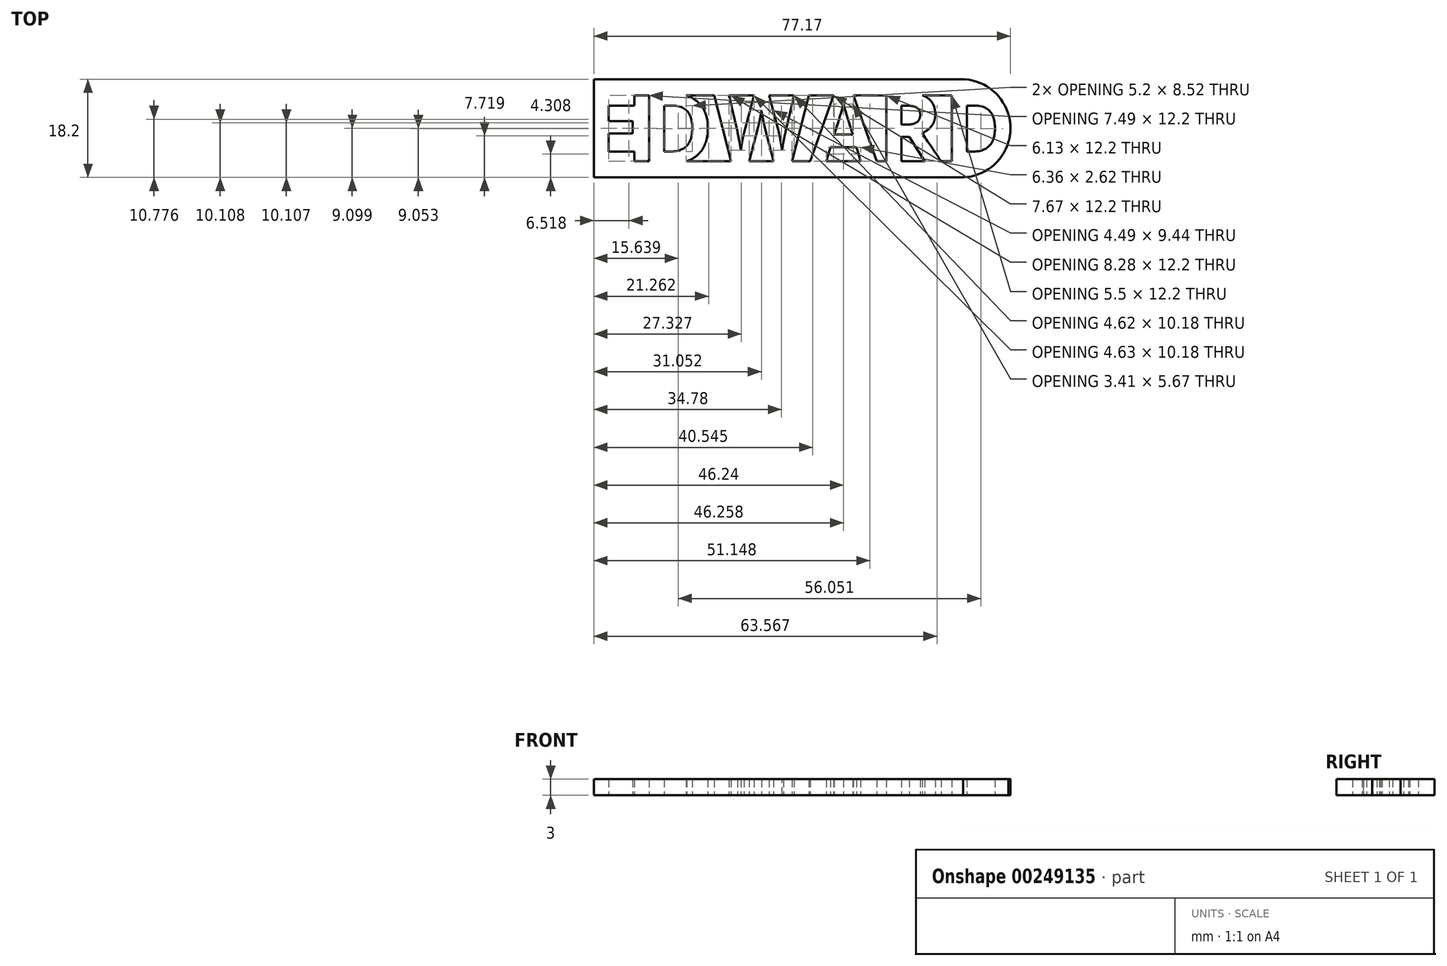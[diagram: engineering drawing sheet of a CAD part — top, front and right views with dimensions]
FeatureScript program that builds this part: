
annotation { "Feature Type Name" : "Feature", "Feature Type Description" : "" }
export const myFeature = defineFeature(function(context is Context, id is Id, definition is map)
    precondition{}
    {
        {
            var Q0;
            Q0=qCreatedBy(makeId("Top.planeOp"),FACE);
            var sketch = newSketch(context, id + "F0", { "sketchPlane" : qUnion([Q0])});
            skText(sketch, "E0", { "text": "EDWARD", "fontName": "OpenSans-Bold.ttf"});
            skLineSegment(sketch, "E1.bottom", {"start": v(-40, 0.5) * mm, "end": v(40, 0.5) * mm});
            skLineSegment(sketch, "E1.top", {"start": v(-40, -2.5) * mm, "end": v(40, -2.5) * mm});
            skLineSegment(sketch, "E1.left", {"start": v(-40, -2.5) * mm, "end": v(-40, 0.5) * mm});
            skLineSegment(sketch, "E1.right", {"start": v(40, -2.5) * mm, "end": v(40, 0.5) * mm});
            skLineSegment(sketch, "E2.bottom", {"start": v(-40, 12.7) * mm, "end": v(40, 12.7) * mm});
            skLineSegment(sketch, "E2.top", {"start": v(-40, 15.7) * mm, "end": v(40, 15.7) * mm});
            skLineSegment(sketch, "E2.left", {"start": v(-40, 12.7) * mm, "end": v(-40, 15.7) * mm});
            skLineSegment(sketch, "E2.right", {"start": v(40, 12.7) * mm, "end": v(40, 15.7) * mm});
            const initialGuessF0  = {"E0": [-0.04, 0, 1, 0, 0.0132]};
            skSetInitialGuess(sketch, initialGuessF0);
            skSolve(sketch);
        }
        {
            var Q0;
            {var subQ0=sQuery(id+"F0.wireOp",EDGE,"E0.sketch_text.stroke-0");Q0=makeQuery(id+"F0.imprint","IMPRINT",FACE,{"disambiguationData":[TD([[makeQuery(id+"F0.imprint","IMPRINT",EDGE,{"derivedFrom":subQ0}),-1.0]])]});}
            var Q1;
            {var subQ8=sQuery(id+"F0.wireOp",EDGE,"E0.sketch_text.stroke-4");Q1=makeQuery(id+"F0.imprint","IMPRINT",FACE,{"disambiguationData":[TD([[makeQuery(id+"F0.imprint","IMPRINT",EDGE,{"derivedFrom":subQ8}),-1.0]])]});}
            var Q2;
            {var subQ27=sQuery(id+"F0.wireOp",EDGE,"E0.sketch_text.stroke-0");Q2=makeQuery(id+"F0.imprint","IMPRINT",FACE,{"disambiguationData":[TD([[makeQuery(id+"F0.imprint","IMPRINT",EDGE,{"derivedFrom":subQ27}),1.0]])]});}
            var Q3;
            {var subQ1=sQuery(id+"F0.wireOp",EDGE,"E0.sketch_text.stroke-12");Q3=makeQuery(id+"F0.imprint","IMPRINT",FACE,{"disambiguationData":[TD([[makeQuery(id+"F0.imprint","IMPRINT",EDGE,{"derivedFrom":subQ1}),-1.0]])]});}
            var Q4;
            {var subQ0=sQuery(id+"F0.wireOp",EDGE,"E0.sketch_text.stroke-14");Q4=makeQuery(id+"F0.imprint","IMPRINT",FACE,{"disambiguationData":[TD([[makeQuery(id+"F0.imprint","IMPRINT",EDGE,{"derivedFrom":subQ0}),-1.0]])]});}
            var Q5;
            {var subQ11=sQuery(id+"F0.wireOp",EDGE,"E0.sketch_text.stroke-26");Q5=makeQuery(id+"F0.imprint","IMPRINT",FACE,{"disambiguationData":[TD([[makeQuery(id+"F0.imprint","IMPRINT",EDGE,{"derivedFrom":subQ11}),-1.0]])]});}
            var Q6;
            {var subQ0=sQuery(id+"F0.wireOp",EDGE,"E0.sketch_text.stroke-31");Q6=makeQuery(id+"F0.imprint","IMPRINT",FACE,{"disambiguationData":[TD([[makeQuery(id+"F0.imprint","IMPRINT",EDGE,{"derivedFrom":subQ0}),-1.0]])]});}
            var Q7;
            {var subQ0=sQuery(id+"F0.wireOp",EDGE,"E0.sketch_text.stroke-24");Q7=makeQuery(id+"F0.imprint","IMPRINT",FACE,{"disambiguationData":[TD([[makeQuery(id+"F0.imprint","IMPRINT",EDGE,{"derivedFrom":subQ0}),-1.0]])]});}
            var Q8;
            {var subQ5=sQuery(id+"F0.wireOp",EDGE,"E0.sketch_text.stroke-49");Q8=makeQuery(id+"F0.imprint","IMPRINT",FACE,{"disambiguationData":[TD([[makeQuery(id+"F0.imprint","IMPRINT",EDGE,{"derivedFrom":subQ5}),-1.0]])]});}
            var Q9;
            {var subQ0=sQuery(id+"F0.wireOp",EDGE,"E0.sketch_text.stroke-51");Q9=makeQuery(id+"F0.imprint","IMPRINT",FACE,{"disambiguationData":[TD([[makeQuery(id+"F0.imprint","IMPRINT",EDGE,{"derivedFrom":subQ0}),-1.0]])]});}
            var Q10;
            {var subQ0=sQuery(id+"F0.wireOp",EDGE,"E0.sketch_text.stroke-55");Q10=makeQuery(id+"F0.imprint","IMPRINT",FACE,{"disambiguationData":[TD([[makeQuery(id+"F0.imprint","IMPRINT",EDGE,{"derivedFrom":subQ0}),-1.0]])]});}
            var Q11;
            Q11=makeQuery(id+"F0.imprint","IMPRINT",FACE,{"disambiguationData":[TD([[makeQuery(id+"F0.imprint","IMPRINT",EDGE,{"derivedFrom":sQuery(id+"F0.wireOp",EDGE,"E0.sketch_text.stroke-60")}),-1.0]])]});
            var Q12;
            {var subQ0=sQuery(id+"F0.wireOp",EDGE,"E0.sketch_text.stroke-68");Q12=makeQuery(id+"F0.imprint","IMPRINT",FACE,{"disambiguationData":[TD([[makeQuery(id+"F0.imprint","IMPRINT",EDGE,{"derivedFrom":subQ0}),-1.0]])]});}
            var Q13;
            {var subQ0=sQuery(id+"F0.wireOp",EDGE,"E0.sketch_text.stroke-76");Q13=makeQuery(id+"F0.imprint","IMPRINT",FACE,{"disambiguationData":[TD([[makeQuery(id+"F0.imprint","IMPRINT",EDGE,{"derivedFrom":subQ0}),-1.0]])]});}
            var Q14;
            {var subQ0=sQuery(id+"F0.wireOp",EDGE,"E0.sketch_text.stroke-81");Q14=makeQuery(id+"F0.imprint","IMPRINT",FACE,{"disambiguationData":[TD([[makeQuery(id+"F0.imprint","IMPRINT",EDGE,{"derivedFrom":subQ0}),-1.0]])]});}
            var Q15;
            {var subQ1=sQuery(id+"F0.wireOp",EDGE,"E0.sketch_text.stroke-79");Q15=makeQuery(id+"F0.imprint","IMPRINT",FACE,{"disambiguationData":[TD([[makeQuery(id+"F0.imprint","IMPRINT",EDGE,{"derivedFrom":subQ1}),-1.0]])]});}
            var Q16;
            {var subQ37=sQuery(id+"F0.wireOp",EDGE,"E0.sketch_text.stroke-2");Q16=makeQuery(id+"F0.imprint","IMPRINT",FACE,{"disambiguationData":[TD([[makeQuery(id+"F0.imprint","IMPRINT",EDGE,{"derivedFrom":subQ37}),1.0]])]});}
            var Q17;
            {var subQ0=sQuery(id+"F0.wireOp",EDGE,"E0.sketch_text.stroke-83");Q17=makeQuery(id+"F0.imprint","IMPRINT",FACE,{"disambiguationData":[TD([[makeQuery(id+"F0.imprint","IMPRINT",EDGE,{"derivedFrom":subQ0}),-1.0]])]});}
            var Q18;
            {var subQ0=sQuery(id+"F0.wireOp",EDGE,"E0.sketch_text.stroke-70");Q18=makeQuery(id+"F0.imprint","IMPRINT",FACE,{"disambiguationData":[TD([[makeQuery(id+"F0.imprint","IMPRINT",EDGE,{"derivedFrom":subQ0}),-1.0]])]});}
            var Q19;
            {var subQ0=sQuery(id+"F0.wireOp",EDGE,"E0.sketch_text.stroke-53");Q19=makeQuery(id+"F0.imprint","IMPRINT",FACE,{"disambiguationData":[TD([[makeQuery(id+"F0.imprint","IMPRINT",EDGE,{"derivedFrom":subQ0}),-1.0]])]});}
            var Q20;
            {var subQ0=sQuery(id+"F0.wireOp",EDGE,"E0.sketch_text.stroke-46");Q20=makeQuery(id+"F0.imprint","IMPRINT",FACE,{"disambiguationData":[TD([[makeQuery(id+"F0.imprint","IMPRINT",EDGE,{"derivedFrom":subQ0}),-1.0]])]});}
            var Q21;
            {var subQ0=sQuery(id+"F0.wireOp",EDGE,"E0.sketch_text.stroke-39");Q21=makeQuery(id+"F0.imprint","IMPRINT",FACE,{"disambiguationData":[TD([[makeQuery(id+"F0.imprint","IMPRINT",EDGE,{"derivedFrom":subQ0}),-1.0]])]});}
            var Q22;
            {var subQ0=sQuery(id+"F0.wireOp",EDGE,"E0.sketch_text.stroke-33");Q22=makeQuery(id+"F0.imprint","IMPRINT",FACE,{"disambiguationData":[TD([[makeQuery(id+"F0.imprint","IMPRINT",EDGE,{"derivedFrom":subQ0}),-1.0]])]});}
            var Q23;
            {var subQ0=sQuery(id+"F0.wireOp",EDGE,"E0.sketch_text.stroke-16");Q23=makeQuery(id+"F0.imprint","IMPRINT",FACE,{"disambiguationData":[TD([[makeQuery(id+"F0.imprint","IMPRINT",EDGE,{"derivedFrom":subQ0}),-1.0]])]});}
            var Q24;
            {var subQ0=sQuery(id+"F0.wireOp",EDGE,"E0.sketch_text.stroke-2");Q24=makeQuery(id+"F0.imprint","IMPRINT",FACE,{"disambiguationData":[TD([[makeQuery(id+"F0.imprint","IMPRINT",EDGE,{"derivedFrom":subQ0}),-1.0]])]});}
            extrude(context, id + "F1", {"entities" : qUnion([Q0, Q1, Q2, Q3, Q4, Q5, Q6, Q7, Q8, Q9, Q10, Q11, Q12, Q13, Q14, Q15, Q16, Q17, Q18, Q19, Q20, Q21, Q22, Q23, Q24]), "depth" : 2 * mm});
        }
        {
            var Q0;
            Q0=makeQuery(id+"F1.opExtrude","SWEPT_FACE",FACE,{"disambiguationData":[OSD([sQuery(id+"F0.wireOp",EDGE,"E2.left")])]});
            var Q1;
            Q1=makeQuery(id+"F1.opExtrude","SWEPT_FACE",FACE,{"disambiguationData":[OSD([sQuery(id+"F0.wireOp",EDGE,"E0.sketch_text.stroke-1")])]});
            extrude(context, id + "F2", {"entities" : qUnion([Q0]), "operationType" : NewBodyOperationType.REMOVE, "endBound" : BoundingType.UP_TO_SURFACE, "oppositeDirection" : true, "endBoundEntityFace" : qUnion([Q1]), "depth" : 25 * mm});
        }
        {
            var Q0;
            Q0=makeQuery(id+"F1.opExtrude","SWEPT_FACE",FACE,{"disambiguationData":[OSD([sQuery(id+"F0.wireOp",EDGE,"E1.left")])]});
            var Q1;
            {var subQ0=sQuery(id+"F0.wireOp",EDGE,"E0.sketch_text.stroke-1");Q1=makeQuery(id+"F2.boolean.opBoolean","MERGE",FACE,{"derivedFrom":[makeQuery(id+"F1.opExtrude","SWEPT_FACE",FACE,{"disambiguationData":[OSD([subQ0])]}),makeQuery(id+"F2.opExtrude","CAP_FACE",FACE,{"disambiguationData":[OSD([subQ0])],"isStart":false})]});}
            extrude(context, id + "F3", {"entities" : qUnion([Q0]), "operationType" : NewBodyOperationType.REMOVE, "endBound" : BoundingType.UP_TO_SURFACE, "oppositeDirection" : true, "endBoundEntityFace" : qUnion([Q1]), "depth" : 25 * mm});
        }
        {
            var Q0;
            Q0=makeQuery(id+"F1.opExtrude","CAP_FACE",FACE,{"disambiguationData":[OSD([sQuery(id+"F0.wireOp",EDGE,"E0.sketch_text.stroke-1"),sQuery(id+"F0.wireOp",EDGE,"E0.sketch_text.stroke-3"),sQuery(id+"F0.wireOp",EDGE,"E0.sketch_text.stroke-4"),sQuery(id+"F0.wireOp",EDGE,"E0.sketch_text.stroke-5"),sQuery(id+"F0.wireOp",EDGE,"E0.sketch_text.stroke-6"),sQuery(id+"F0.wireOp",EDGE,"E0.sketch_text.stroke-7"),sQuery(id+"F0.wireOp",EDGE,"E0.sketch_text.stroke-8"),sQuery(id+"F0.wireOp",EDGE,"E0.sketch_text.stroke-9"),sQuery(id+"F0.wireOp",EDGE,"E0.sketch_text.stroke-10"),sQuery(id+"F0.wireOp",EDGE,"E0.sketch_text.stroke-11"),sQuery(id+"F0.wireOp",EDGE,"E0.sketch_text.stroke-12"),sQuery(id+"F0.wireOp",EDGE,"E0.sketch_text.stroke-13"),sQuery(id+"F0.wireOp",EDGE,"E0.sketch_text.stroke-15"),sQuery(id+"F0.wireOp",EDGE,"E0.sketch_text.stroke-17"),sQuery(id+"F0.wireOp",EDGE,"E0.sketch_text.stroke-18"),sQuery(id+"F0.wireOp",EDGE,"E0.sketch_text.stroke-19"),sQuery(id+"F0.wireOp",EDGE,"E0.sketch_text.stroke-20"),sQuery(id+"F0.wireOp",EDGE,"E0.sketch_text.stroke-21"),sQuery(id+"F0.wireOp",EDGE,"E0.sketch_text.stroke-22"),sQuery(id+"F0.wireOp",EDGE,"E0.sketch_text.stroke-23"),sQuery(id+"F0.wireOp",EDGE,"E0.sketch_text.stroke-25"),sQuery(id+"F0.wireOp",EDGE,"E0.sketch_text.stroke-26"),sQuery(id+"F0.wireOp",EDGE,"E0.sketch_text.stroke-27"),sQuery(id+"F0.wireOp",EDGE,"E0.sketch_text.stroke-28"),sQuery(id+"F0.wireOp",EDGE,"E0.sketch_text.stroke-29"),sQuery(id+"F0.wireOp",EDGE,"E0.sketch_text.stroke-30"),sQuery(id+"F0.wireOp",EDGE,"E0.sketch_text.stroke-32"),sQuery(id+"F0.wireOp",EDGE,"E0.sketch_text.stroke-34"),sQuery(id+"F0.wireOp",EDGE,"E0.sketch_text.stroke-35"),sQuery(id+"F0.wireOp",EDGE,"E0.sketch_text.stroke-36"),sQuery(id+"F0.wireOp",EDGE,"E0.sketch_text.stroke-37"),sQuery(id+"F0.wireOp",EDGE,"E0.sketch_text.stroke-38"),sQuery(id+"F0.wireOp",EDGE,"E0.sketch_text.stroke-40"),sQuery(id+"F0.wireOp",EDGE,"E0.sketch_text.stroke-41"),sQuery(id+"F0.wireOp",EDGE,"E0.sketch_text.stroke-42"),sQuery(id+"F0.wireOp",EDGE,"E0.sketch_text.stroke-43"),sQuery(id+"F0.wireOp",EDGE,"E0.sketch_text.stroke-44"),sQuery(id+"F0.wireOp",EDGE,"E0.sketch_text.stroke-45"),sQuery(id+"F0.wireOp",EDGE,"E0.sketch_text.stroke-47"),sQuery(id+"F0.wireOp",EDGE,"E0.sketch_text.stroke-48"),sQuery(id+"F0.wireOp",EDGE,"E0.sketch_text.stroke-49"),sQuery(id+"F0.wireOp",EDGE,"E0.sketch_text.stroke-50"),sQuery(id+"F0.wireOp",EDGE,"E0.sketch_text.stroke-52"),sQuery(id+"F0.wireOp",EDGE,"E0.sketch_text.stroke-54"),sQuery(id+"F0.wireOp",EDGE,"E0.sketch_text.stroke-56"),sQuery(id+"F0.wireOp",EDGE,"E0.sketch_text.stroke-57"),sQuery(id+"F0.wireOp",EDGE,"E0.sketch_text.stroke-58"),sQuery(id+"F0.wireOp",EDGE,"E0.sketch_text.stroke-59"),sQuery(id+"F0.wireOp",EDGE,"E0.sketch_text.stroke-60"),sQuery(id+"F0.wireOp",EDGE,"E0.sketch_text.stroke-61"),sQuery(id+"F0.wireOp",EDGE,"E0.sketch_text.stroke-62"),sQuery(id+"F0.wireOp",EDGE,"E0.sketch_text.stroke-63"),sQuery(id+"F0.wireOp",EDGE,"E0.sketch_text.stroke-64"),sQuery(id+"F0.wireOp",EDGE,"E0.sketch_text.stroke-65"),sQuery(id+"F0.wireOp",EDGE,"E0.sketch_text.stroke-66"),sQuery(id+"F0.wireOp",EDGE,"E0.sketch_text.stroke-67"),sQuery(id+"F0.wireOp",EDGE,"E0.sketch_text.stroke-69"),sQuery(id+"F0.wireOp",EDGE,"E0.sketch_text.stroke-71"),sQuery(id+"F0.wireOp",EDGE,"E0.sketch_text.stroke-72"),sQuery(id+"F0.wireOp",EDGE,"E0.sketch_text.stroke-73"),sQuery(id+"F0.wireOp",EDGE,"E0.sketch_text.stroke-74"),sQuery(id+"F0.wireOp",EDGE,"E0.sketch_text.stroke-75"),sQuery(id+"F0.wireOp",EDGE,"E0.sketch_text.stroke-77"),sQuery(id+"F0.wireOp",EDGE,"E0.sketch_text.stroke-78"),sQuery(id+"F0.wireOp",EDGE,"E0.sketch_text.stroke-79"),sQuery(id+"F0.wireOp",EDGE,"E0.sketch_text.stroke-80"),sQuery(id+"F0.wireOp",EDGE,"E0.sketch_text.stroke-82"),sQuery(id+"F0.wireOp",EDGE,"E0.sketch_text.stroke-84"),sQuery(id+"F0.wireOp",EDGE,"E0.sketch_text.stroke-85"),sQuery(id+"F0.wireOp",EDGE,"E0.sketch_text.stroke-86"),sQuery(id+"F0.wireOp",EDGE,"E0.sketch_text.stroke-87"),sQuery(id+"F0.wireOp",EDGE,"E0.sketch_text.stroke-88"),sQuery(id+"F0.wireOp",EDGE,"E0.sketch_text.stroke-89"),sQuery(id+"F0.wireOp",EDGE,"E0.sketch_text.stroke-90"),sQuery(id+"F0.wireOp",EDGE,"E1.bottom"),sQuery(id+"F0.wireOp",EDGE,"E1.top"),sQuery(id+"F0.wireOp",EDGE,"E1.left"),sQuery(id+"F0.wireOp",EDGE,"E1.right"),sQuery(id+"F0.wireOp",EDGE,"E2.bottom"),sQuery(id+"F0.wireOp",EDGE,"E2.top"),sQuery(id+"F0.wireOp",EDGE,"E2.left"),sQuery(id+"F0.wireOp",EDGE,"E2.right")])],"isStart":false});
            var sketch = newSketch(context, id + "F4", { "sketchPlane" : qUnion([Q0])});
            skCircle(sketch, "E3", {"center": v(29.7, 6.6) * mm, "radius": 9.1 * mm});
            skSolve(sketch);
        }
        {
            var Q0;
            {var subQ4=sQuery(id+"F0.wireOp",EDGE,"E0.sketch_text.stroke-84");var subQ7=makeQuery(id+"F1.opExtrude","CAP_EDGE",EDGE,{"disambiguationData":[OSD([subQ4])],"isStart":false});Q0=makeQuery(id+"F4.imprint","IMPRINT",FACE,{"disambiguationData":[TD([[makeQuery(id+"F4.imprint","IMPRINT",EDGE,{"derivedFrom":subQ7}),1.0]])]});}
            var Q1;
            {var subQ2=sQuery(id+"F0.wireOp",EDGE,"E0.sketch_text.stroke-80");var subQ7=makeQuery(id+"F1.opExtrude","CAP_EDGE",EDGE,{"disambiguationData":[OSD([subQ2])],"isStart":false});Q1=makeQuery(id+"F4.imprint","IMPRINT",FACE,{"disambiguationData":[TD([[makeQuery(id+"F4.imprint","IMPRINT",EDGE,{"derivedFrom":subQ7}),1.0]])]});}
            var Q2;
            Q2=makeQuery(id+"F1.opExtrude","CAP_FACE",FACE,{"disambiguationData":[OSD([sQuery(id+"F0.wireOp",EDGE,"E0.sketch_text.stroke-1"),sQuery(id+"F0.wireOp",EDGE,"E0.sketch_text.stroke-3"),sQuery(id+"F0.wireOp",EDGE,"E0.sketch_text.stroke-4"),sQuery(id+"F0.wireOp",EDGE,"E0.sketch_text.stroke-5"),sQuery(id+"F0.wireOp",EDGE,"E0.sketch_text.stroke-6"),sQuery(id+"F0.wireOp",EDGE,"E0.sketch_text.stroke-7"),sQuery(id+"F0.wireOp",EDGE,"E0.sketch_text.stroke-8"),sQuery(id+"F0.wireOp",EDGE,"E0.sketch_text.stroke-9"),sQuery(id+"F0.wireOp",EDGE,"E0.sketch_text.stroke-10"),sQuery(id+"F0.wireOp",EDGE,"E0.sketch_text.stroke-11"),sQuery(id+"F0.wireOp",EDGE,"E0.sketch_text.stroke-12"),sQuery(id+"F0.wireOp",EDGE,"E0.sketch_text.stroke-13"),sQuery(id+"F0.wireOp",EDGE,"E0.sketch_text.stroke-15"),sQuery(id+"F0.wireOp",EDGE,"E0.sketch_text.stroke-17"),sQuery(id+"F0.wireOp",EDGE,"E0.sketch_text.stroke-18"),sQuery(id+"F0.wireOp",EDGE,"E0.sketch_text.stroke-19"),sQuery(id+"F0.wireOp",EDGE,"E0.sketch_text.stroke-20"),sQuery(id+"F0.wireOp",EDGE,"E0.sketch_text.stroke-21"),sQuery(id+"F0.wireOp",EDGE,"E0.sketch_text.stroke-22"),sQuery(id+"F0.wireOp",EDGE,"E0.sketch_text.stroke-23"),sQuery(id+"F0.wireOp",EDGE,"E0.sketch_text.stroke-25"),sQuery(id+"F0.wireOp",EDGE,"E0.sketch_text.stroke-26"),sQuery(id+"F0.wireOp",EDGE,"E0.sketch_text.stroke-27"),sQuery(id+"F0.wireOp",EDGE,"E0.sketch_text.stroke-28"),sQuery(id+"F0.wireOp",EDGE,"E0.sketch_text.stroke-29"),sQuery(id+"F0.wireOp",EDGE,"E0.sketch_text.stroke-30"),sQuery(id+"F0.wireOp",EDGE,"E0.sketch_text.stroke-32"),sQuery(id+"F0.wireOp",EDGE,"E0.sketch_text.stroke-34"),sQuery(id+"F0.wireOp",EDGE,"E0.sketch_text.stroke-35"),sQuery(id+"F0.wireOp",EDGE,"E0.sketch_text.stroke-36"),sQuery(id+"F0.wireOp",EDGE,"E0.sketch_text.stroke-37"),sQuery(id+"F0.wireOp",EDGE,"E0.sketch_text.stroke-38"),sQuery(id+"F0.wireOp",EDGE,"E0.sketch_text.stroke-40"),sQuery(id+"F0.wireOp",EDGE,"E0.sketch_text.stroke-41"),sQuery(id+"F0.wireOp",EDGE,"E0.sketch_text.stroke-42"),sQuery(id+"F0.wireOp",EDGE,"E0.sketch_text.stroke-43"),sQuery(id+"F0.wireOp",EDGE,"E0.sketch_text.stroke-44"),sQuery(id+"F0.wireOp",EDGE,"E0.sketch_text.stroke-45"),sQuery(id+"F0.wireOp",EDGE,"E0.sketch_text.stroke-47"),sQuery(id+"F0.wireOp",EDGE,"E0.sketch_text.stroke-48"),sQuery(id+"F0.wireOp",EDGE,"E0.sketch_text.stroke-49"),sQuery(id+"F0.wireOp",EDGE,"E0.sketch_text.stroke-50"),sQuery(id+"F0.wireOp",EDGE,"E0.sketch_text.stroke-52"),sQuery(id+"F0.wireOp",EDGE,"E0.sketch_text.stroke-54"),sQuery(id+"F0.wireOp",EDGE,"E0.sketch_text.stroke-56"),sQuery(id+"F0.wireOp",EDGE,"E0.sketch_text.stroke-57"),sQuery(id+"F0.wireOp",EDGE,"E0.sketch_text.stroke-58"),sQuery(id+"F0.wireOp",EDGE,"E0.sketch_text.stroke-59"),sQuery(id+"F0.wireOp",EDGE,"E0.sketch_text.stroke-60"),sQuery(id+"F0.wireOp",EDGE,"E0.sketch_text.stroke-61"),sQuery(id+"F0.wireOp",EDGE,"E0.sketch_text.stroke-62"),sQuery(id+"F0.wireOp",EDGE,"E0.sketch_text.stroke-63"),sQuery(id+"F0.wireOp",EDGE,"E0.sketch_text.stroke-64"),sQuery(id+"F0.wireOp",EDGE,"E0.sketch_text.stroke-65"),sQuery(id+"F0.wireOp",EDGE,"E0.sketch_text.stroke-66"),sQuery(id+"F0.wireOp",EDGE,"E0.sketch_text.stroke-67"),sQuery(id+"F0.wireOp",EDGE,"E0.sketch_text.stroke-69"),sQuery(id+"F0.wireOp",EDGE,"E0.sketch_text.stroke-71"),sQuery(id+"F0.wireOp",EDGE,"E0.sketch_text.stroke-72"),sQuery(id+"F0.wireOp",EDGE,"E0.sketch_text.stroke-73"),sQuery(id+"F0.wireOp",EDGE,"E0.sketch_text.stroke-74"),sQuery(id+"F0.wireOp",EDGE,"E0.sketch_text.stroke-75"),sQuery(id+"F0.wireOp",EDGE,"E0.sketch_text.stroke-77"),sQuery(id+"F0.wireOp",EDGE,"E0.sketch_text.stroke-78"),sQuery(id+"F0.wireOp",EDGE,"E0.sketch_text.stroke-79"),sQuery(id+"F0.wireOp",EDGE,"E0.sketch_text.stroke-80"),sQuery(id+"F0.wireOp",EDGE,"E0.sketch_text.stroke-82"),sQuery(id+"F0.wireOp",EDGE,"E0.sketch_text.stroke-84"),sQuery(id+"F0.wireOp",EDGE,"E0.sketch_text.stroke-85"),sQuery(id+"F0.wireOp",EDGE,"E0.sketch_text.stroke-86"),sQuery(id+"F0.wireOp",EDGE,"E0.sketch_text.stroke-87"),sQuery(id+"F0.wireOp",EDGE,"E0.sketch_text.stroke-88"),sQuery(id+"F0.wireOp",EDGE,"E0.sketch_text.stroke-89"),sQuery(id+"F0.wireOp",EDGE,"E0.sketch_text.stroke-90"),sQuery(id+"F0.wireOp",EDGE,"E1.bottom"),sQuery(id+"F0.wireOp",EDGE,"E1.top"),sQuery(id+"F0.wireOp",EDGE,"E1.left"),sQuery(id+"F0.wireOp",EDGE,"E1.right"),sQuery(id+"F0.wireOp",EDGE,"E2.bottom"),sQuery(id+"F0.wireOp",EDGE,"E2.top"),sQuery(id+"F0.wireOp",EDGE,"E2.left"),sQuery(id+"F0.wireOp",EDGE,"E2.right")])],"isStart":true});
            extrude(context, id + "F5", {"entities" : qUnion([Q0, Q1]), "operationType" : NewBodyOperationType.ADD, "endBound" : BoundingType.UP_TO_SURFACE, "oppositeDirection" : true, "endBoundEntityFace" : qUnion([Q2]), "depth" : 25 * mm});
        }
        {
            var Q0;
            {var subQ1=sQuery(id+"F0.wireOp",EDGE,"E2.right");var subQ7=makeQuery(id+"F1.opExtrude","CAP_EDGE",EDGE,{"disambiguationData":[OSD([subQ1])],"isStart":false});Q0=makeQuery(id+"F4.imprint","IMPRINT",FACE,{"disambiguationData":[TD([[makeQuery(id+"F4.imprint","IMPRINT",EDGE,{"derivedFrom":subQ7}),1.0]])]});}
            var Q1;
            {var subQ3=sQuery(id+"F0.wireOp",EDGE,"E1.right");var subQ7=makeQuery(id+"F1.opExtrude","CAP_EDGE",EDGE,{"disambiguationData":[OSD([subQ3])],"isStart":false});Q1=makeQuery(id+"F4.imprint","IMPRINT",FACE,{"disambiguationData":[TD([[makeQuery(id+"F4.imprint","IMPRINT",EDGE,{"derivedFrom":subQ7}),1.0]])]});}
            var Q2;
            {var subQ0=sQuery(id+"F4.wireOp",EDGE,"E3");var subQ1=sQuery(id+"F0.wireOp",EDGE,"E1.bottom");var subQ2=sQuery(id+"F0.wireOp",EDGE,"E0.sketch_text.stroke-80");var subQ3=sQuery(id+"F0.wireOp",EDGE,"E0.sketch_text.stroke-79");var subQ4=sQuery(id+"F0.wireOp",EDGE,"E2.right");var subQ5=sQuery(id+"F0.wireOp",EDGE,"E2.left");var subQ6=sQuery(id+"F0.wireOp",EDGE,"E2.top");var subQ7=sQuery(id+"F0.wireOp",EDGE,"E2.bottom");var subQ8=sQuery(id+"F0.wireOp",EDGE,"E1.right");var subQ9=sQuery(id+"F0.wireOp",EDGE,"E1.left");var subQ10=sQuery(id+"F0.wireOp",EDGE,"E1.top");var subQ11=sQuery(id+"F0.wireOp",EDGE,"E0.sketch_text.stroke-90");var subQ12=sQuery(id+"F0.wireOp",EDGE,"E0.sketch_text.stroke-89");var subQ13=sQuery(id+"F0.wireOp",EDGE,"E0.sketch_text.stroke-88");var subQ14=sQuery(id+"F0.wireOp",EDGE,"E0.sketch_text.stroke-87");var subQ15=sQuery(id+"F0.wireOp",EDGE,"E0.sketch_text.stroke-86");var subQ16=sQuery(id+"F0.wireOp",EDGE,"E0.sketch_text.stroke-85");var subQ17=sQuery(id+"F0.wireOp",EDGE,"E0.sketch_text.stroke-84");var subQ18=sQuery(id+"F0.wireOp",EDGE,"E0.sketch_text.stroke-82");var subQ19=sQuery(id+"F0.wireOp",EDGE,"E0.sketch_text.stroke-78");var subQ20=sQuery(id+"F0.wireOp",EDGE,"E0.sketch_text.stroke-77");var subQ21=sQuery(id+"F0.wireOp",EDGE,"E0.sketch_text.stroke-75");var subQ22=sQuery(id+"F0.wireOp",EDGE,"E0.sketch_text.stroke-74");var subQ23=sQuery(id+"F0.wireOp",EDGE,"E0.sketch_text.stroke-73");var subQ24=sQuery(id+"F0.wireOp",EDGE,"E0.sketch_text.stroke-72");var subQ25=sQuery(id+"F0.wireOp",EDGE,"E0.sketch_text.stroke-71");var subQ26=sQuery(id+"F0.wireOp",EDGE,"E0.sketch_text.stroke-69");var subQ27=sQuery(id+"F0.wireOp",EDGE,"E0.sketch_text.stroke-67");var subQ28=sQuery(id+"F0.wireOp",EDGE,"E0.sketch_text.stroke-66");var subQ29=sQuery(id+"F0.wireOp",EDGE,"E0.sketch_text.stroke-65");var subQ30=sQuery(id+"F0.wireOp",EDGE,"E0.sketch_text.stroke-64");var subQ31=sQuery(id+"F0.wireOp",EDGE,"E0.sketch_text.stroke-63");var subQ32=sQuery(id+"F0.wireOp",EDGE,"E0.sketch_text.stroke-62");var subQ33=sQuery(id+"F0.wireOp",EDGE,"E0.sketch_text.stroke-61");var subQ34=sQuery(id+"F0.wireOp",EDGE,"E0.sketch_text.stroke-60");var subQ35=sQuery(id+"F0.wireOp",EDGE,"E0.sketch_text.stroke-59");var subQ36=sQuery(id+"F0.wireOp",EDGE,"E0.sketch_text.stroke-58");var subQ37=sQuery(id+"F0.wireOp",EDGE,"E0.sketch_text.stroke-57");var subQ38=sQuery(id+"F0.wireOp",EDGE,"E0.sketch_text.stroke-56");var subQ39=sQuery(id+"F0.wireOp",EDGE,"E0.sketch_text.stroke-54");var subQ40=sQuery(id+"F0.wireOp",EDGE,"E0.sketch_text.stroke-52");var subQ41=sQuery(id+"F0.wireOp",EDGE,"E0.sketch_text.stroke-50");var subQ42=sQuery(id+"F0.wireOp",EDGE,"E0.sketch_text.stroke-49");var subQ43=sQuery(id+"F0.wireOp",EDGE,"E0.sketch_text.stroke-48");var subQ44=sQuery(id+"F0.wireOp",EDGE,"E0.sketch_text.stroke-47");var subQ45=sQuery(id+"F0.wireOp",EDGE,"E0.sketch_text.stroke-45");var subQ46=sQuery(id+"F0.wireOp",EDGE,"E0.sketch_text.stroke-44");var subQ47=sQuery(id+"F0.wireOp",EDGE,"E0.sketch_text.stroke-43");var subQ48=sQuery(id+"F0.wireOp",EDGE,"E0.sketch_text.stroke-42");var subQ49=sQuery(id+"F0.wireOp",EDGE,"E0.sketch_text.stroke-41");var subQ50=sQuery(id+"F0.wireOp",EDGE,"E0.sketch_text.stroke-40");var subQ51=sQuery(id+"F0.wireOp",EDGE,"E0.sketch_text.stroke-38");var subQ52=sQuery(id+"F0.wireOp",EDGE,"E0.sketch_text.stroke-37");var subQ53=sQuery(id+"F0.wireOp",EDGE,"E0.sketch_text.stroke-36");var subQ54=sQuery(id+"F0.wireOp",EDGE,"E0.sketch_text.stroke-35");var subQ55=sQuery(id+"F0.wireOp",EDGE,"E0.sketch_text.stroke-34");var subQ56=sQuery(id+"F0.wireOp",EDGE,"E0.sketch_text.stroke-32");var subQ57=sQuery(id+"F0.wireOp",EDGE,"E0.sketch_text.stroke-30");var subQ58=sQuery(id+"F0.wireOp",EDGE,"E0.sketch_text.stroke-29");var subQ59=sQuery(id+"F0.wireOp",EDGE,"E0.sketch_text.stroke-28");var subQ60=sQuery(id+"F0.wireOp",EDGE,"E0.sketch_text.stroke-27");var subQ61=sQuery(id+"F0.wireOp",EDGE,"E0.sketch_text.stroke-26");var subQ62=sQuery(id+"F0.wireOp",EDGE,"E0.sketch_text.stroke-25");var subQ63=sQuery(id+"F0.wireOp",EDGE,"E0.sketch_text.stroke-23");var subQ64=sQuery(id+"F0.wireOp",EDGE,"E0.sketch_text.stroke-22");var subQ65=sQuery(id+"F0.wireOp",EDGE,"E0.sketch_text.stroke-21");var subQ66=sQuery(id+"F0.wireOp",EDGE,"E0.sketch_text.stroke-20");var subQ67=sQuery(id+"F0.wireOp",EDGE,"E0.sketch_text.stroke-19");var subQ68=sQuery(id+"F0.wireOp",EDGE,"E0.sketch_text.stroke-18");var subQ69=sQuery(id+"F0.wireOp",EDGE,"E0.sketch_text.stroke-17");var subQ70=sQuery(id+"F0.wireOp",EDGE,"E0.sketch_text.stroke-15");var subQ71=sQuery(id+"F0.wireOp",EDGE,"E0.sketch_text.stroke-13");var subQ72=sQuery(id+"F0.wireOp",EDGE,"E0.sketch_text.stroke-12");var subQ73=sQuery(id+"F0.wireOp",EDGE,"E0.sketch_text.stroke-11");var subQ74=sQuery(id+"F0.wireOp",EDGE,"E0.sketch_text.stroke-10");var subQ75=sQuery(id+"F0.wireOp",EDGE,"E0.sketch_text.stroke-9");var subQ76=sQuery(id+"F0.wireOp",EDGE,"E0.sketch_text.stroke-8");var subQ77=sQuery(id+"F0.wireOp",EDGE,"E0.sketch_text.stroke-7");var subQ78=sQuery(id+"F0.wireOp",EDGE,"E0.sketch_text.stroke-6");var subQ79=sQuery(id+"F0.wireOp",EDGE,"E0.sketch_text.stroke-5");var subQ80=sQuery(id+"F0.wireOp",EDGE,"E0.sketch_text.stroke-4");var subQ81=sQuery(id+"F0.wireOp",EDGE,"E0.sketch_text.stroke-3");var subQ82=sQuery(id+"F0.wireOp",EDGE,"E0.sketch_text.stroke-1");Q2=makeQuery(id+"F5.boolean.opBoolean","MERGE",FACE,{"derivedFrom":[makeQuery(id+"F1.opExtrude","CAP_FACE",FACE,{"disambiguationData":[OSD([subQ82,subQ81,subQ80,subQ79,subQ78,subQ77,subQ76,subQ75,subQ74,subQ73,subQ72,subQ71,subQ70,subQ69,subQ68,subQ67,subQ66,subQ65,subQ64,subQ63,subQ62,subQ61,subQ60,subQ59,subQ58,subQ57,subQ56,subQ55,subQ54,subQ53,subQ52,subQ51,subQ50,subQ49,subQ48,subQ47,subQ46,subQ45,subQ44,subQ43,subQ42,subQ41,subQ40,subQ39,subQ38,subQ37,subQ36,subQ35,subQ34,subQ33,subQ32,subQ31,subQ30,subQ29,subQ28,subQ27,subQ26,subQ25,subQ24,subQ23,subQ22,subQ21,subQ20,subQ19,subQ3,subQ2,subQ18,subQ17,subQ16,subQ15,subQ14,subQ13,subQ12,subQ11,subQ1,subQ10,subQ9,subQ8,subQ7,subQ6,subQ5,subQ4])],"isStart":true}),makeQuery(id+"F5.opExtrude","CAP_FACE",FACE,{"disambiguationData":[OSD([subQ82,subQ81,subQ80,subQ79,subQ78,subQ77,subQ76,subQ75,subQ74,subQ73,subQ72,subQ71,subQ70,subQ69,subQ68,subQ67,subQ66,subQ65,subQ64,subQ63,subQ62,subQ61,subQ60,subQ59,subQ58,subQ57,subQ56,subQ55,subQ54,subQ53,subQ52,subQ51,subQ50,subQ49,subQ48,subQ47,subQ46,subQ45,subQ44,subQ43,subQ42,subQ41,subQ40,subQ39,subQ38,subQ37,subQ36,subQ35,subQ34,subQ33,subQ32,subQ31,subQ30,subQ29,subQ28,subQ27,subQ26,subQ25,subQ24,subQ23,subQ22,subQ21,subQ20,subQ19,subQ3,subQ2,subQ18,subQ17,subQ16,subQ15,subQ14,subQ13,subQ12,subQ11,subQ1,subQ10,subQ9,subQ8,subQ7,subQ6,subQ5,subQ4]),ownerDisambiguation([makeQuery(id+"F5.opExtrude","SWEPT_BODY",BODY,{"disambiguationData":[OSD([subQ17,subQ16,subQ7,subQ0])]})])],"isStart":false}),makeQuery(id+"F5.opExtrude","CAP_FACE",FACE,{"disambiguationData":[OSD([subQ82,subQ81,subQ80,subQ79,subQ78,subQ77,subQ76,subQ75,subQ74,subQ73,subQ72,subQ71,subQ70,subQ69,subQ68,subQ67,subQ66,subQ65,subQ64,subQ63,subQ62,subQ61,subQ60,subQ59,subQ58,subQ57,subQ56,subQ55,subQ54,subQ53,subQ52,subQ51,subQ50,subQ49,subQ48,subQ47,subQ46,subQ45,subQ44,subQ43,subQ42,subQ41,subQ40,subQ39,subQ38,subQ37,subQ36,subQ35,subQ34,subQ33,subQ32,subQ31,subQ30,subQ29,subQ28,subQ27,subQ26,subQ25,subQ24,subQ23,subQ22,subQ21,subQ20,subQ19,subQ3,subQ2,subQ18,subQ17,subQ16,subQ15,subQ14,subQ13,subQ12,subQ11,subQ1,subQ10,subQ9,subQ8,subQ7,subQ6,subQ5,subQ4]),ownerDisambiguation([makeQuery(id+"F5.opExtrude","SWEPT_BODY",BODY,{"disambiguationData":[OSD([subQ3,subQ2,subQ1,subQ0])]})])],"isStart":false})]});}
            extrude(context, id + "F6", {"entities" : qUnion([Q0, Q1]), "operationType" : NewBodyOperationType.REMOVE, "endBound" : BoundingType.UP_TO_SURFACE, "oppositeDirection" : true, "endBoundEntityFace" : qUnion([Q2]), "depth" : 25 * mm});
        }
        {
            var Q0;
            {var subQ0=sQuery(id+"F4.wireOp",EDGE,"E3");var subQ1=sQuery(id+"F0.wireOp",EDGE,"E1.bottom");var subQ2=sQuery(id+"F0.wireOp",EDGE,"E0.sketch_text.stroke-80");var subQ3=sQuery(id+"F0.wireOp",EDGE,"E0.sketch_text.stroke-79");var subQ4=sQuery(id+"F0.wireOp",EDGE,"E2.bottom");var subQ5=sQuery(id+"F0.wireOp",EDGE,"E0.sketch_text.stroke-85");var subQ6=sQuery(id+"F0.wireOp",EDGE,"E0.sketch_text.stroke-84");Q0=makeQuery(id+"F5.boolean.opBoolean","MERGE",FACE,{"derivedFrom":[makeQuery(id+"F1.opExtrude","CAP_FACE",FACE,{"disambiguationData":[OSD([sQuery(id+"F0.wireOp",EDGE,"E0.sketch_text.stroke-1"),sQuery(id+"F0.wireOp",EDGE,"E0.sketch_text.stroke-3"),sQuery(id+"F0.wireOp",EDGE,"E0.sketch_text.stroke-4"),sQuery(id+"F0.wireOp",EDGE,"E0.sketch_text.stroke-5"),sQuery(id+"F0.wireOp",EDGE,"E0.sketch_text.stroke-6"),sQuery(id+"F0.wireOp",EDGE,"E0.sketch_text.stroke-7"),sQuery(id+"F0.wireOp",EDGE,"E0.sketch_text.stroke-8"),sQuery(id+"F0.wireOp",EDGE,"E0.sketch_text.stroke-9"),sQuery(id+"F0.wireOp",EDGE,"E0.sketch_text.stroke-10"),sQuery(id+"F0.wireOp",EDGE,"E0.sketch_text.stroke-11"),sQuery(id+"F0.wireOp",EDGE,"E0.sketch_text.stroke-12"),sQuery(id+"F0.wireOp",EDGE,"E0.sketch_text.stroke-13"),sQuery(id+"F0.wireOp",EDGE,"E0.sketch_text.stroke-15"),sQuery(id+"F0.wireOp",EDGE,"E0.sketch_text.stroke-17"),sQuery(id+"F0.wireOp",EDGE,"E0.sketch_text.stroke-18"),sQuery(id+"F0.wireOp",EDGE,"E0.sketch_text.stroke-19"),sQuery(id+"F0.wireOp",EDGE,"E0.sketch_text.stroke-20"),sQuery(id+"F0.wireOp",EDGE,"E0.sketch_text.stroke-21"),sQuery(id+"F0.wireOp",EDGE,"E0.sketch_text.stroke-22"),sQuery(id+"F0.wireOp",EDGE,"E0.sketch_text.stroke-23"),sQuery(id+"F0.wireOp",EDGE,"E0.sketch_text.stroke-25"),sQuery(id+"F0.wireOp",EDGE,"E0.sketch_text.stroke-26"),sQuery(id+"F0.wireOp",EDGE,"E0.sketch_text.stroke-27"),sQuery(id+"F0.wireOp",EDGE,"E0.sketch_text.stroke-28"),sQuery(id+"F0.wireOp",EDGE,"E0.sketch_text.stroke-29"),sQuery(id+"F0.wireOp",EDGE,"E0.sketch_text.stroke-30"),sQuery(id+"F0.wireOp",EDGE,"E0.sketch_text.stroke-32"),sQuery(id+"F0.wireOp",EDGE,"E0.sketch_text.stroke-34"),sQuery(id+"F0.wireOp",EDGE,"E0.sketch_text.stroke-35"),sQuery(id+"F0.wireOp",EDGE,"E0.sketch_text.stroke-36"),sQuery(id+"F0.wireOp",EDGE,"E0.sketch_text.stroke-37"),sQuery(id+"F0.wireOp",EDGE,"E0.sketch_text.stroke-38"),sQuery(id+"F0.wireOp",EDGE,"E0.sketch_text.stroke-40"),sQuery(id+"F0.wireOp",EDGE,"E0.sketch_text.stroke-41"),sQuery(id+"F0.wireOp",EDGE,"E0.sketch_text.stroke-42"),sQuery(id+"F0.wireOp",EDGE,"E0.sketch_text.stroke-43"),sQuery(id+"F0.wireOp",EDGE,"E0.sketch_text.stroke-44"),sQuery(id+"F0.wireOp",EDGE,"E0.sketch_text.stroke-45"),sQuery(id+"F0.wireOp",EDGE,"E0.sketch_text.stroke-47"),sQuery(id+"F0.wireOp",EDGE,"E0.sketch_text.stroke-48"),sQuery(id+"F0.wireOp",EDGE,"E0.sketch_text.stroke-49"),sQuery(id+"F0.wireOp",EDGE,"E0.sketch_text.stroke-50"),sQuery(id+"F0.wireOp",EDGE,"E0.sketch_text.stroke-52"),sQuery(id+"F0.wireOp",EDGE,"E0.sketch_text.stroke-54"),sQuery(id+"F0.wireOp",EDGE,"E0.sketch_text.stroke-56"),sQuery(id+"F0.wireOp",EDGE,"E0.sketch_text.stroke-57"),sQuery(id+"F0.wireOp",EDGE,"E0.sketch_text.stroke-58"),sQuery(id+"F0.wireOp",EDGE,"E0.sketch_text.stroke-59"),sQuery(id+"F0.wireOp",EDGE,"E0.sketch_text.stroke-60"),sQuery(id+"F0.wireOp",EDGE,"E0.sketch_text.stroke-61"),sQuery(id+"F0.wireOp",EDGE,"E0.sketch_text.stroke-62"),sQuery(id+"F0.wireOp",EDGE,"E0.sketch_text.stroke-63"),sQuery(id+"F0.wireOp",EDGE,"E0.sketch_text.stroke-64"),sQuery(id+"F0.wireOp",EDGE,"E0.sketch_text.stroke-65"),sQuery(id+"F0.wireOp",EDGE,"E0.sketch_text.stroke-66"),sQuery(id+"F0.wireOp",EDGE,"E0.sketch_text.stroke-67"),sQuery(id+"F0.wireOp",EDGE,"E0.sketch_text.stroke-69"),sQuery(id+"F0.wireOp",EDGE,"E0.sketch_text.stroke-71"),sQuery(id+"F0.wireOp",EDGE,"E0.sketch_text.stroke-72"),sQuery(id+"F0.wireOp",EDGE,"E0.sketch_text.stroke-73"),sQuery(id+"F0.wireOp",EDGE,"E0.sketch_text.stroke-74"),sQuery(id+"F0.wireOp",EDGE,"E0.sketch_text.stroke-75"),sQuery(id+"F0.wireOp",EDGE,"E0.sketch_text.stroke-77"),sQuery(id+"F0.wireOp",EDGE,"E0.sketch_text.stroke-78"),subQ3,subQ2,sQuery(id+"F0.wireOp",EDGE,"E0.sketch_text.stroke-82"),subQ6,subQ5,sQuery(id+"F0.wireOp",EDGE,"E0.sketch_text.stroke-86"),sQuery(id+"F0.wireOp",EDGE,"E0.sketch_text.stroke-87"),sQuery(id+"F0.wireOp",EDGE,"E0.sketch_text.stroke-88"),sQuery(id+"F0.wireOp",EDGE,"E0.sketch_text.stroke-89"),sQuery(id+"F0.wireOp",EDGE,"E0.sketch_text.stroke-90"),subQ1,sQuery(id+"F0.wireOp",EDGE,"E1.top"),sQuery(id+"F0.wireOp",EDGE,"E1.left"),sQuery(id+"F0.wireOp",EDGE,"E1.right"),subQ4,sQuery(id+"F0.wireOp",EDGE,"E2.top"),sQuery(id+"F0.wireOp",EDGE,"E2.left"),sQuery(id+"F0.wireOp",EDGE,"E2.right")])],"isStart":false}),makeQuery(id+"F5.opExtrude","CAP_FACE",FACE,{"disambiguationData":[OSD([subQ6,subQ5,subQ4,subQ0])],"isStart":true}),makeQuery(id+"F5.opExtrude","CAP_FACE",FACE,{"disambiguationData":[OSD([subQ3,subQ2,subQ1,subQ0])],"isStart":true})]});}
            extrude(context, id + "F7", {"entities" : qUnion([Q0]), "operationType" : NewBodyOperationType.ADD, "depth" : 1 * mm});
        }
    });
